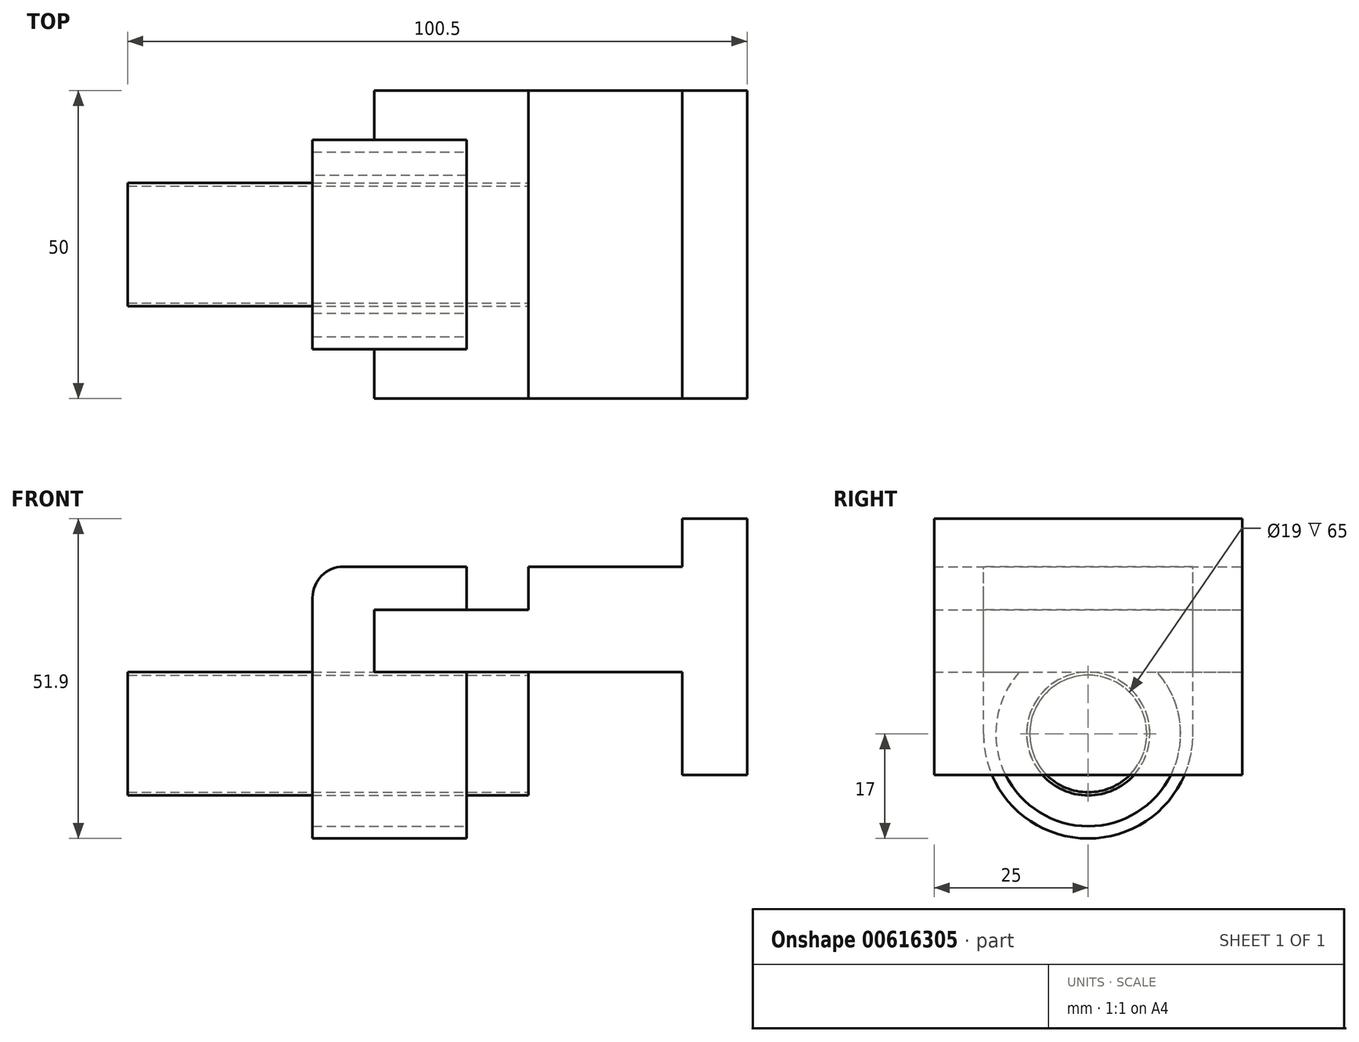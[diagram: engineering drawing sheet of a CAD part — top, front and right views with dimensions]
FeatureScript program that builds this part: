
annotation { "Feature Type Name" : "Feature", "Feature Type Description" : "" }
export const myFeature = defineFeature(function(context is Context, id is Id, definition is map)
    precondition{}
    {
        {
            var Q0;
            Q0=qCreatedBy(makeId("Front.planeOp"),FACE);
            var sketch = newSketch(context, id + "F0", { "sketchPlane" : qUnion([Q0])});
            skLineSegment(sketch, "E0.bottom", {"start": v(-30.5, 5.1) * mm, "end": v(30, 5.1) * mm});
            skLineSegment(sketch, "E0.top", {"start": v(-30.5, -5) * mm, "end": v(30, -5) * mm});
            skLineSegment(sketch, "E0.left", {"start": v(-30.5, 5.1) * mm, "end": v(-30.5, -5) * mm});
            skPoint(sketch, "E0.middle", {"position": v(0, 0) * mm});
            skLineSegment(sketch, "E1.bottom", {"start": v(-5.5, 5.1) * mm, "end": v(30, 5.1) * mm});
            skLineSegment(sketch, "E1.top", {"start": v(-5.5, 12.1) * mm, "end": v(30, 12.1) * mm});
            skLineSegment(sketch, "E1.left", {"start": v(-5.5, 5.1) * mm, "end": v(-5.5, 12.1) * mm});
            skLineSegment(sketch, "E2", {"start": v(19.5, 5.1) * mm, "end": v(19.5, 12.1) * mm});
            skLineSegment(sketch, "E3", {"start": v(30, -5) * mm, "end": v(30, 19.9) * mm});
            skLineSegment(sketch, "E4", {"start": v(30, 19.9) * mm, "end": v(19.5, 19.9) * mm});
            skLineSegment(sketch, "E5", {"start": v(19.5, 19.9) * mm, "end": v(19.5, -5) * mm});
            skLineSegment(sketch, "E6.bottom", {"start": v(19.5, -5) * mm, "end": v(30, -5) * mm});
            skLineSegment(sketch, "E6.top", {"start": v(19.5, -21.67) * mm, "end": v(30, -21.67) * mm});
            skLineSegment(sketch, "E6.left", {"start": v(19.5, -5) * mm, "end": v(19.5, -21.67) * mm});
            skLineSegment(sketch, "E6.right", {"start": v(30, -5) * mm, "end": v(30, -21.67) * mm});
            skSolve(sketch);
        }
        {
            var Q0;
            {var subQ0=sQuery(id+"F0.wireOp",EDGE,"E0.left");var subQ5=sQuery(id+"F0.wireOp",EDGE,"E2");var subQ6=sQuery(id+"F0.wireOp",EDGE,"E0.bottom");var subQ9=sQuery(id+"F0.wireOp",EDGE,"E1.left");var subQ12=sQuery(id+"F0.wireOp",EDGE,"E3");var subQ13=makeQuery(id+"F0.imprint","INTERSECT",VERTEX,{"derivedFrom":[subQ6,subQ12]});var subQ14=makeQuery(id+"F0.imprint","IMPRINT",EDGE,{"disambiguationData":[TD([[subQ13,1.0]])],"derivedFrom":subQ6});var subQ19=makeQuery(id+"F0.imprint","IMPRINT",EDGE,{"derivedFrom":subQ5});var subQ20=sQuery(id+"F0.wireOp",EDGE,"E4");Q0=qUnion([makeQuery(id+"F0.imprint","IMPRINT",FACE,{"disambiguationData":[TD([[makeQuery(id+"F0.imprint","IMPRINT",EDGE,{"derivedFrom":subQ9}),-1.0]])]}),makeQuery(id+"F0.imprint","IMPRINT",FACE,{"disambiguationData":[TD([[makeQuery(id+"F0.imprint","IMPRINT",EDGE,{"derivedFrom":sQuery(id+"F0.wireOp",EDGE,"E6.top")}),1.0]])]}),makeQuery(id+"F0.imprint","IMPRINT",FACE,{"disambiguationData":[TD([[subQ14,-1.0]])]}),makeQuery(id+"F0.imprint","IMPRINT",FACE,{"disambiguationData":[TD([[makeQuery(id+"F0.imprint","IMPRINT",EDGE,{"derivedFrom":subQ20}),1.0]])]}),makeQuery(id+"F0.imprint","IMPRINT",FACE,{"disambiguationData":[TD([[subQ19,-1.0]])]}),makeQuery(id+"F0.imprint","IMPRINT",FACE,{"disambiguationData":[TD([[makeQuery(id+"F0.imprint","IMPRINT",EDGE,{"derivedFrom":subQ0}),1.0]])]})]);}
            extrude(context, id + "F1", {"entities" : qUnion([Q0]), "depth" : 25 * mm, "offsetDistance" : 25 * mm, "hasSecondDirection" : true, "secondDirectionOppositeDirection" : true, "secondDirectionDepth" : 25 * mm});
        }
        {
            var Q0;
            Q0=makeQuery(id+"F1.opExtrude","SWEPT_FACE",FACE,{"disambiguationData":[OSD([sQuery(id+"F0.wireOp",EDGE,"E0.left")])]});
            var sketch = newSketch(context, id + "F2", { "sketchPlane" : qUnion([Q0])});
            skPoint(sketch, "E7", {"position": v(0, -15) * mm});
            skLineSegment(sketch, "E8.0", {"start": v(25, -5) * mm, "end": v(-25, -5) * mm, "construction": true});
            skCircle(sketch, "E9", {"center": v(0, -15) * mm, "radius": 10 * mm});
            skCircle(sketch, "E10", {"center": v(0, -15) * mm, "radius": 9.5 * mm});
            skSolve(sketch);
        }
        {
            var Q0;
            Q0 = qSketchRegion(id + "F2", true);
            extrude(context, id + "F3", {"entities" : qUnion([Q0]), "depth" : 40 * mm, "offsetDistance" : 25 * mm, "hasSecondDirection" : true, "secondDirectionOppositeDirection" : true, "secondDirectionDepth" : 25 * mm});
        }
        {
            var Q0;
            Q0=makeQuery(id+"F1.opExtrude","SWEPT_FACE",FACE,{"disambiguationData":[OSD([sQuery(id+"F0.wireOp",EDGE,"E0.left")])]});
            var sketch = newSketch(context, id + "F4", { "sketchPlane" : qUnion([Q0])});
            skCircle(sketch, "E11.0", {"center": v(0, -15) * mm, "radius": 10 * mm, "construction": true});
            skLineSegment(sketch, "E12.0", {"start": v(25, -5) * mm, "end": v(-25, -5) * mm, "construction": true});
            skLineSegment(sketch, "E13.0", {"start": v(25, 5.1) * mm, "end": v(-25, 5.1) * mm, "construction": true});
            skCircle(sketch, "E14", {"center": v(0, -15) * mm, "radius": 15 * mm});
            skCircle(sketch, "E15", {"center": v(0, -15) * mm, "radius": 17 * mm});
            skLineSegment(sketch, "E16", {"start": v(0, -15) * mm, "end": v(20.33, -15) * mm, "construction": true});
            skLineSegment(sketch, "E17", {"start": v(17, -15) * mm, "end": v(17, -5) * mm});
            skLineSegment(sketch, "E18", {"start": v(-17, -15) * mm, "end": v(-17, -5) * mm});
            skLineSegment(sketch, "E19", {"start": v(-17, -5) * mm, "end": v(17, -5) * mm});
            skLineSegment(sketch, "E20", {"start": v(-17, -5) * mm, "end": v(-17, 5.1) * mm});
            skLineSegment(sketch, "E21", {"start": v(-17, 5.1) * mm, "end": v(17, 5.1) * mm});
            skLineSegment(sketch, "E22", {"start": v(17, 5.1) * mm, "end": v(17, -5) * mm});
            skLineSegment(sketch, "E23.0", {"start": v(25, 12.1) * mm, "end": v(-25, 12.1) * mm, "construction": true});
            skLineSegment(sketch, "E24", {"start": v(-17, 5.1) * mm, "end": v(-17, 12.1) * mm});
            skLineSegment(sketch, "E25", {"start": v(-17, 12.1) * mm, "end": v(17, 12.1) * mm});
            skLineSegment(sketch, "E26", {"start": v(17, 12.1) * mm, "end": v(17, 5.1) * mm});
            skSolve(sketch);
        }
        {
            var Q0;
            {var subQ3=sQuery(id+"F4.wireOp",EDGE,"E19");var subQ6=sQuery(id+"F4.wireOp",EDGE,"E14");var subQ7=makeQuery(id+"F4.imprint","INTERSECT",VERTEX,{"disambiguationData":[OD(0.0)],"derivedFrom":[subQ6,subQ3]});Q0=makeQuery(id+"F4.imprint","IMPRINT",FACE,{"disambiguationData":[TD([[makeQuery(id+"F4.imprint","IMPRINT",EDGE,{"disambiguationData":[TD([[subQ7,1.0]])],"derivedFrom":subQ6}),-1.0]])]});}
            var Q1;
            {var subQ0=sQuery(id+"F4.wireOp",EDGE,"E18");Q1=makeQuery(id+"F4.imprint","IMPRINT",FACE,{"disambiguationData":[TD([[makeQuery(id+"F4.imprint","IMPRINT",EDGE,{"derivedFrom":subQ0}),-1.0]])]});}
            var Q2;
            {var subQ0=sQuery(id+"F4.wireOp",EDGE,"E17");Q2=makeQuery(id+"F4.imprint","IMPRINT",FACE,{"disambiguationData":[TD([[makeQuery(id+"F4.imprint","IMPRINT",EDGE,{"derivedFrom":subQ0}),1.0]])]});}
            var Q3;
            {var subQ0=sQuery(id+"F4.wireOp",EDGE,"E20");Q3=makeQuery(id+"F4.imprint","IMPRINT",FACE,{"disambiguationData":[TD([[makeQuery(id+"F4.imprint","IMPRINT",EDGE,{"derivedFrom":subQ0}),-1.0]])]});}
            var Q4;
            {var subQ0=sQuery(id+"F4.wireOp",EDGE,"E19");var subQ1=sQuery(id+"F4.wireOp",EDGE,"E14");var subQ2=makeQuery(id+"F4.imprint","INTERSECT",VERTEX,{"disambiguationData":[OD(0.0)],"derivedFrom":[subQ1,subQ0]});Q4=makeQuery(id+"F4.imprint","IMPRINT",FACE,{"disambiguationData":[TD([[makeQuery(id+"F4.imprint","IMPRINT",EDGE,{"disambiguationData":[TD([[subQ2,-1.0]])],"derivedFrom":subQ1}),-1.0]])]});}
            var Q5;
            {var subQ0=sQuery(id+"F4.wireOp",EDGE,"E19");var subQ1=sQuery(id+"F4.wireOp",EDGE,"E14");var subQ2=makeQuery(id+"F4.imprint","INTERSECT",VERTEX,{"disambiguationData":[OD(0.0)],"derivedFrom":[subQ1,subQ0]});Q5=makeQuery(id+"F4.imprint","IMPRINT",FACE,{"disambiguationData":[TD([[makeQuery(id+"F4.imprint","IMPRINT",EDGE,{"disambiguationData":[TD([[subQ2,-1.0]])],"derivedFrom":subQ1}),1.0]])]});}
            var Q6;
            Q6=makeQuery(id+"F4.imprint","IMPRINT",FACE,{"disambiguationData":[TD([[makeQuery(id+"F4.imprint","IMPRINT",EDGE,{"derivedFrom":sQuery(id+"F4.wireOp",EDGE,"E21")}),-1.0]])]});
            extrude(context, id + "F5", {"entities" : qUnion([Q0, Q1, Q2, Q3, Q4, Q5, Q6]), "depth" : 10 * mm, "offsetDistance" : 25 * mm});
        }
        {
            var Q0;
            Q0=makeQuery(id+"F5.opExtrude","CAP_FACE",FACE,{"disambiguationData":[OSD([sQuery(id+"F4.wireOp",EDGE,"E14"),sQuery(id+"F4.wireOp",EDGE,"E15"),sQuery(id+"F4.wireOp",EDGE,"E17"),sQuery(id+"F4.wireOp",EDGE,"E18"),sQuery(id+"F4.wireOp",EDGE,"E19"),sQuery(id+"F4.wireOp",EDGE,"E20"),sQuery(id+"F4.wireOp",EDGE,"E22"),sQuery(id+"F4.wireOp",EDGE,"E24"),sQuery(id+"F4.wireOp",EDGE,"E25"),sQuery(id+"F4.wireOp",EDGE,"E26")])],"isStart":true});
            var sketch = newSketch(context, id + "F6", { "sketchPlane" : qUnion([Q0])});
            skLineSegment(sketch, "E27.0", {"start": v(-25, 12.1) * mm, "end": v(25, 12.1) * mm, "construction": true});
            skLineSegment(sketch, "E28.0", {"start": v(-25, 5.1) * mm, "end": v(25, 5.1) * mm, "construction": true});
            skLineSegment(sketch, "E29.0", {"start": v(17, -15) * mm, "end": v(17, 12.1) * mm, "construction": true});
            skLineSegment(sketch, "E30.0", {"start": v(-17, -15) * mm, "end": v(-17, 12.1) * mm, "construction": true});
            skLineSegment(sketch, "E31.bottom", {"start": v(17, 12.1) * mm, "end": v(-17, 12.1) * mm});
            skLineSegment(sketch, "E31.top", {"start": v(17, 5.1) * mm, "end": v(-17, 5.1) * mm});
            skLineSegment(sketch, "E31.left", {"start": v(17, 12.1) * mm, "end": v(17, 5.1) * mm});
            skLineSegment(sketch, "E31.right", {"start": v(-17, 12.1) * mm, "end": v(-17, 5.1) * mm});
            skArc(sketch, "E32.0", {"start": v(11.18, -5) * mm, "mid": v(0, -30) * mm, "end": v(-11.18, -5) * mm});
            skLineSegment(sketch, "E33.0", {"start": v(-25, -5) * mm, "end": v(25, -5) * mm, "construction": true});
            skPoint(sketch, "E34.0", {"position": v(17, -15) * mm});
            skPoint(sketch, "E35.0", {"position": v(-17, -15) * mm});
            skArc(sketch, "E36.0", {"start": v(17, -15) * mm, "mid": v(0, -32) * mm, "end": v(-17, -15) * mm});
            skArc(sketch, "E37.0.0", {"start": v(-17, -15) * mm, "mid": v(0, -32) * mm, "end": v(17, -15) * mm, "construction": true});
            skLineSegment(sketch, "E37.0.2", {"start": v(17, 12.1) * mm, "end": v(-17, 12.1) * mm, "construction": true});
            skLineSegment(sketch, "E37.0.3", {"start": v(-17, 12.1) * mm, "end": v(-17, -15) * mm, "construction": true});
            skLineSegment(sketch, "E38", {"start": v(-17, -15) * mm, "end": v(-17, -5) * mm});
            skLineSegment(sketch, "E39", {"start": v(-17, -5) * mm, "end": v(17, -5) * mm});
            skLineSegment(sketch, "E40", {"start": v(17, -5) * mm, "end": v(17, -15) * mm});
            skSolve(sketch);
        }
        {
            var Q0;
            Q0=makeQuery(id+"F6.imprint","IMPRINT",FACE,{"disambiguationData":[TD([[makeQuery(id+"F6.imprint","IMPRINT",EDGE,{"derivedFrom":sQuery(id+"F6.wireOp",EDGE,"E31.bottom")}),1.0]])]});
            var Q1;
            {var subQ1=sQuery(id+"F6.wireOp",EDGE,"E32.0");Q1=makeQuery(id+"F6.imprint","IMPRINT",FACE,{"disambiguationData":[TD([[makeQuery(id+"F6.imprint","IMPRINT",EDGE,{"derivedFrom":subQ1}),1.0]])]});}
            extrude(context, id + "F7", {"entities" : qUnion([Q0, Q1]), "operationType" : NewBodyOperationType.ADD, "depth" : 15 * mm, "offsetDistance" : 25 * mm});
        }
        {
            var Q0;
            Q0=makeQuery(id+"F5.opExtrude","CAP_EDGE",EDGE,{"disambiguationData":[OSD([sQuery(id+"F4.wireOp",EDGE,"E25")])],"isStart":false});
            fillet(context, id + "F8", {"entities" : qUnion([Q0]), "radius" : 5 * mm, "tangentPropagation" : true, "allowEdgeOverflow" : false});
        }
    });
